# Revit family: KLS - shelf
name_source: partatom
category: Generic Models
revit_build: Autodesk Revit 2014 (Build: 20130308_1515(x64)
units: mm (PartAtom-declared; Revit-internal decimal feet)

## types (4) — shared parameters
Default Elevation = 1219 mm
hole = 30 mm  [stored 0.0984252 ft]
material = <By Category>

## per-type parameters (varying)
| type | length to wall | shelf length | shelf thickness | thickness around hole |
| KLS - shelf 90cmx3cm | 180 mm  [stored 0.590551 ft] | 900 mm  [stored 2.95276 ft] | 30 mm  [stored 0.0984252 ft] | 30 mm  [stored 0.0984252 ft] |
| KLS - shelf 70cmx3cm | 146 mm | 700 mm  [stored 2.29659 ft] | 30 mm  [stored 0.0984252 ft] | 25 mm  [stored 0.082021 ft] |
| KLS - shelf 50cmx2cm | 146 mm | 500 mm  [stored 1.64042 ft] | 20 mm  [stored 0.0656168 ft] | 22 mm  [stored 0.0721785 ft] |
| KLS - shelf 30cmx2cm | 146 mm | 300 mm | 20 mm  [stored 0.0656168 ft] | 20 mm  [stored 0.0656168 ft] |

note: [stored X ft] marks values corroborated as IEEE doubles in the binary element streams (Revit-internal decimal feet)

## geometry (parser evidence)
native form markers: Sweep x1
no freeform markers — native parametric forms only
